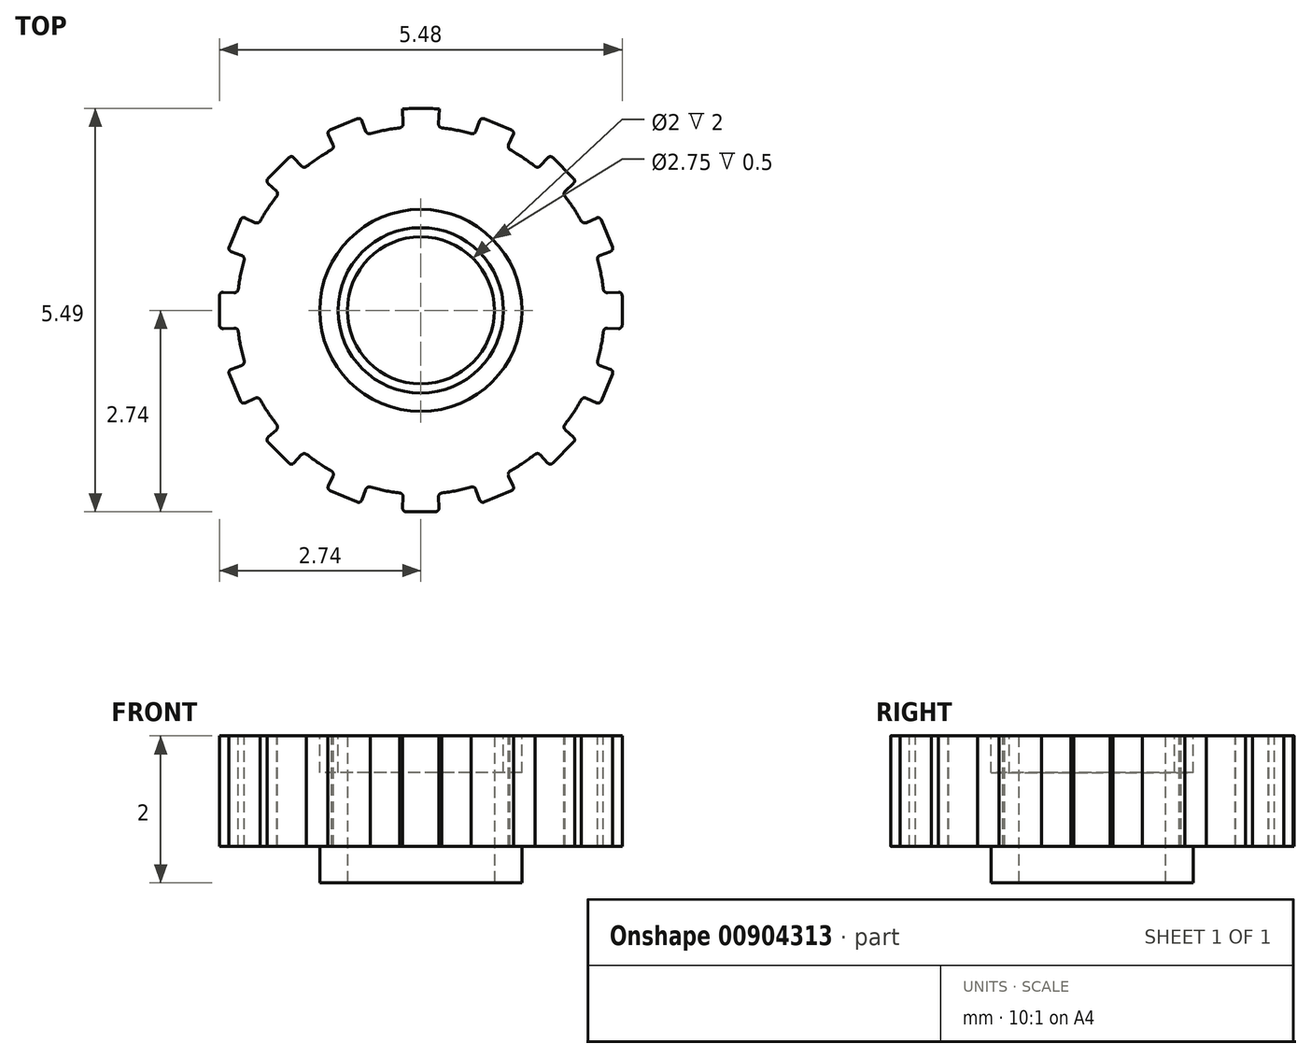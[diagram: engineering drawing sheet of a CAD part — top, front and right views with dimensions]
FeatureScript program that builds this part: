
annotation { "Feature Type Name" : "Feature", "Feature Type Description" : "" }
export const myFeature = defineFeature(function(context is Context, id is Id, definition is map)
    precondition{}
    {
        {
            var Q0;
            Q0=qCreatedBy(makeId("Front.planeOp"),FACE);
            var sketch = newSketch(context, id + "F0", { "sketchPlane" : qUnion([Q0])});
            skLineSegment(sketch, "E0.bottom", {"start": v(0, 0) * mm, "end": v(-2.75, 0) * mm});
            skLineSegment(sketch, "E0.top", {"start": v(0, 2) * mm, "end": v(-2.75, 2) * mm});
            skLineSegment(sketch, "E0.left", {"start": v(0, 0) * mm, "end": v(0, 2) * mm});
            skLineSegment(sketch, "E0.right", {"start": v(-2.75, 0) * mm, "end": v(-2.75, 2) * mm});
            skLineSegment(sketch, "E1", {"start": v(-1, 2) * mm, "end": v(-1, 0) * mm});
            skSolve(sketch);
        }
        {
            var Q0;
            {var subQ0=sQuery(id+"F0.wireOp",EDGE,"E0.right");Q0=makeQuery(id+"F0.imprint","IMPRINT",FACE,{"disambiguationData":[TD([[makeQuery(id+"F0.imprint","IMPRINT",EDGE,{"derivedFrom":subQ0}),-1.0]])]});}
            var Q1;
            Q1=sQuery(id+"F0.wireOp",EDGE,"E0.left");
            revolve(context, id + "F1", {"surfaceOperationType" : NewSurfaceOperationType.NEW, "entities" : qUnion([Q0]), "axis" : qUnion([Q1]), "revolveType" : RevolveType.FULL});
        }
        {
            var Q0;
            Q0=makeQuery(id+"F1.opRevolve","SWEPT_FACE",FACE,{"disambiguationData":[OSD([sQuery(id+"F0.wireOp",EDGE,"E0.top")])]});
            var sketch = newSketch(context, id + "F2", { "sketchPlane" : qUnion([Q0])});
            skLineSegment(sketch, "E2", {"start": v(0, 0) * mm, "end": v(0, 2.75) * mm});
            skLineSegment(sketch, "E3", {"start": v(0, 2.74) * mm, "end": v(-0.25, 2.74) * mm});
            skLineSegment(sketch, "E4", {"start": v(-0.25, 2.74) * mm, "end": v(0.25, 2.74) * mm});
            skLineSegment(sketch, "E5.bottom", {"start": v(0.12, 0) * mm, "end": v(-0.12, 0) * mm});
            skLineSegment(sketch, "E5.top", {"start": v(0.12, 0) * mm, "end": v(-0.12, 0) * mm});
            skLineSegment(sketch, "E5.left", {"start": v(0.12, 0) * mm, "end": v(0.12, 0) * mm});
            skLineSegment(sketch, "E5.right", {"start": v(-0.12, 0) * mm, "end": v(-0.12, 0) * mm});
            skPoint(sketch, "E5.middle", {"position": v(0, 0) * mm});
            skLineSegment(sketch, "E6", {"start": v(-0.25, 2.74) * mm, "end": v(-0.12, 0) * mm});
            skLineSegment(sketch, "E7", {"start": v(0.25, 2.74) * mm, "end": v(0.12, 0) * mm});
            skCircle(sketch, "E8", {"center": v(0, 0) * mm, "radius": 2.5 * mm});
            skLineSegment(sketch, "E9", {"start": v(-0.25, 2.74) * mm, "end": v(-0.2, 2.74) * mm});
            skLineSegment(sketch, "E10", {"start": v(-0.2, 2.74) * mm, "end": v(0.2, 2.74) * mm});
            skLineSegment(sketch, "E11", {"start": v(0.2, 2.74) * mm, "end": v(0.25, 2.74) * mm});
            skLineSegment(sketch, "E12", {"start": v(-0.2, 2.74) * mm, "end": v(-0.12, 0) * mm});
            skLineSegment(sketch, "E13", {"start": v(0.2, 2.74) * mm, "end": v(0.12, 0) * mm});
            skLineSegment(sketch, "E14", {"start": v(-0.25, 2.69) * mm, "end": v(0.25, 2.69) * mm});
            skLineSegment(sketch, "E15", {"start": v(-0.25, 2.69) * mm, "end": v(-0.3, 2.69) * mm});
            skLineSegment(sketch, "E16", {"start": v(0.25, 2.69) * mm, "end": v(0.3, 2.69) * mm});
            skLineSegment(sketch, "E17", {"start": v(-0.3, 2.69) * mm, "end": v(-0.12, 0) * mm});
            skLineSegment(sketch, "E18", {"start": v(0.3, 2.69) * mm, "end": v(0.12, 0) * mm});
            skLineSegment(sketch, "E19", {"start": v(-0.24, 2.54) * mm, "end": v(0.2, 2.54) * mm});
            skLineSegment(sketch, "E20", {"start": v(0.2, 2.54) * mm, "end": v(0.24, 2.54) * mm});
            skLineSegment(sketch, "E21", {"start": v(0.24, 2.54) * mm, "end": v(-0.2, 2.54) * mm});
            skArc(sketch, "E22", {"start": v(-0.28, 2.48) * mm, "mid": v(-0.25, 2.5) * mm, "end": v(-0.24, 2.54) * mm});
            skArc(sketch, "E23", {"start": v(-0.2, 2.74) * mm, "mid": v(-0.23, 2.72) * mm, "end": v(-0.25, 2.69) * mm});
            skArc(sketch, "E24", {"start": v(0.25, 2.69) * mm, "mid": v(0.23, 2.72) * mm, "end": v(0.2, 2.74) * mm});
            skArc(sketch, "E25", {"start": v(0.24, 2.54) * mm, "mid": v(0.25, 2.5) * mm, "end": v(0.28, 2.48) * mm});
            skArc(sketch, "E26.1.0", {"start": v(-1.21, 2.19) * mm, "mid": v(-1.2, 2.22) * mm, "end": v(-1.2, 2.25) * mm});
            skLineSegment(sketch, "E26.1.1", {"start": v(-1.28, 2.43) * mm, "end": v(-0.12, -0.05) * mm});
            skArc(sketch, "E26.1.2", {"start": v(-1.23, 2.45) * mm, "mid": v(-1.26, 2.43) * mm, "end": v(-1.26, 2.39) * mm});
            skLineSegment(sketch, "E26.1.3", {"start": v(-1.28, 2.43) * mm, "end": v(-0.82, 2.63) * mm});
            skArc(sketch, "E26.1.4", {"start": v(-0.8, 2.58) * mm, "mid": v(-0.83, 2.6) * mm, "end": v(-0.86, 2.6) * mm});
            skLineSegment(sketch, "E26.1.5", {"start": v(-0.82, 2.63) * mm, "end": v(0.12, 0.05) * mm});
            skArc(sketch, "E26.1.6", {"start": v(-0.75, 2.44) * mm, "mid": v(-0.72, 2.4) * mm, "end": v(-0.69, 2.4) * mm});
            skArc(sketch, "E26.2.0", {"start": v(-1.96, 1.56) * mm, "mid": v(-1.95, 1.6) * mm, "end": v(-1.97, 1.62) * mm});
            skLineSegment(sketch, "E26.2.1", {"start": v(-2.11, 1.76) * mm, "end": v(-0.09, -0.09) * mm});
            skArc(sketch, "E26.2.2", {"start": v(-2.08, 1.8) * mm, "mid": v(-2.1, 1.76) * mm, "end": v(-2.08, 1.73) * mm});
            skLineSegment(sketch, "E26.2.3", {"start": v(-2.11, 1.76) * mm, "end": v(-1.76, 2.11) * mm});
            skArc(sketch, "E26.2.4", {"start": v(-1.73, 2.08) * mm, "mid": v(-1.76, 2.1) * mm, "end": v(-1.8, 2.08) * mm});
            skLineSegment(sketch, "E26.2.5", {"start": v(-1.76, 2.11) * mm, "end": v(0.09, 0.09) * mm});
            skArc(sketch, "E26.2.6", {"start": v(-1.62, 1.97) * mm, "mid": v(-1.6, 1.95) * mm, "end": v(-1.56, 1.96) * mm});
            skArc(sketch, "E27.2.3.0", {"start": v(-2.4, 0.69) * mm, "mid": v(-2.4, 0.72) * mm, "end": v(-2.44, 0.75) * mm});
            skLineSegment(sketch, "E27.4.3.0", {"start": v(-2.63, 0.82) * mm, "end": v(-0.05, -0.12) * mm});
            skArc(sketch, "E27.7.3.0", {"start": v(-2.6, 0.86) * mm, "mid": v(-2.6, 0.83) * mm, "end": v(-2.58, 0.8) * mm});
            skLineSegment(sketch, "E27.11.3.0", {"start": v(-2.63, 0.82) * mm, "end": v(-2.43, 1.28) * mm});
            skArc(sketch, "E27.14.3.0", {"start": v(-2.39, 1.26) * mm, "mid": v(-2.43, 1.26) * mm, "end": v(-2.45, 1.23) * mm});
            skLineSegment(sketch, "E27.18.3.0", {"start": v(-2.43, 1.28) * mm, "end": v(0.05, 0.12) * mm});
            skArc(sketch, "E27.21.3.0", {"start": v(-2.25, 1.2) * mm, "mid": v(-2.22, 1.2) * mm, "end": v(-2.19, 1.21) * mm});
            skArc(sketch, "E27.2.4.0", {"start": v(-2.48, -0.28) * mm, "mid": v(-2.5, -0.25) * mm, "end": v(-2.54, -0.24) * mm});
            skLineSegment(sketch, "E27.4.4.0", {"start": v(-2.74, -0.25) * mm, "end": v(0, -0.12) * mm});
            skArc(sketch, "E27.7.4.0", {"start": v(-2.74, -0.2) * mm, "mid": v(-2.72, -0.23) * mm, "end": v(-2.69, -0.25) * mm});
            skLineSegment(sketch, "E27.11.4.0", {"start": v(-2.74, -0.25) * mm, "end": v(-2.74, 0.25) * mm});
            skArc(sketch, "E27.14.4.0", {"start": v(-2.69, 0.25) * mm, "mid": v(-2.72, 0.23) * mm, "end": v(-2.74, 0.2) * mm});
            skLineSegment(sketch, "E27.18.4.0", {"start": v(-2.74, 0.25) * mm, "end": v(0, 0.12) * mm});
            skArc(sketch, "E27.21.4.0", {"start": v(-2.54, 0.24) * mm, "mid": v(-2.5, 0.25) * mm, "end": v(-2.48, 0.28) * mm});
            skArc(sketch, "E27.2.5.0", {"start": v(-2.19, -1.21) * mm, "mid": v(-2.22, -1.2) * mm, "end": v(-2.25, -1.2) * mm});
            skLineSegment(sketch, "E27.4.5.0", {"start": v(-2.43, -1.28) * mm, "end": v(0.05, -0.12) * mm});
            skArc(sketch, "E27.7.5.0", {"start": v(-2.45, -1.23) * mm, "mid": v(-2.43, -1.26) * mm, "end": v(-2.39, -1.26) * mm});
            skLineSegment(sketch, "E27.11.5.0", {"start": v(-2.43, -1.28) * mm, "end": v(-2.63, -0.82) * mm});
            skArc(sketch, "E27.14.5.0", {"start": v(-2.58, -0.8) * mm, "mid": v(-2.6, -0.83) * mm, "end": v(-2.6, -0.86) * mm});
            skLineSegment(sketch, "E27.18.5.0", {"start": v(-2.63, -0.82) * mm, "end": v(-0.05, 0.12) * mm});
            skArc(sketch, "E27.21.5.0", {"start": v(-2.44, -0.75) * mm, "mid": v(-2.4, -0.72) * mm, "end": v(-2.4, -0.69) * mm});
            skArc(sketch, "E27.2.6.0", {"start": v(-1.56, -1.96) * mm, "mid": v(-1.6, -1.95) * mm, "end": v(-1.62, -1.97) * mm});
            skLineSegment(sketch, "E27.4.6.0", {"start": v(-1.76, -2.11) * mm, "end": v(0.09, -0.09) * mm});
            skArc(sketch, "E27.7.6.0", {"start": v(-1.8, -2.08) * mm, "mid": v(-1.76, -2.1) * mm, "end": v(-1.73, -2.08) * mm});
            skLineSegment(sketch, "E27.11.6.0", {"start": v(-1.76, -2.11) * mm, "end": v(-2.11, -1.76) * mm});
            skArc(sketch, "E27.14.6.0", {"start": v(-2.08, -1.73) * mm, "mid": v(-2.1, -1.76) * mm, "end": v(-2.08, -1.8) * mm});
            skLineSegment(sketch, "E27.18.6.0", {"start": v(-2.11, -1.76) * mm, "end": v(-0.09, 0.09) * mm});
            skArc(sketch, "E27.21.6.0", {"start": v(-1.97, -1.62) * mm, "mid": v(-1.95, -1.6) * mm, "end": v(-1.96, -1.56) * mm});
            skArc(sketch, "E27.2.7.0", {"start": v(-0.69, -2.4) * mm, "mid": v(-0.72, -2.4) * mm, "end": v(-0.75, -2.44) * mm});
            skLineSegment(sketch, "E27.4.7.0", {"start": v(-0.82, -2.63) * mm, "end": v(0.12, -0.05) * mm});
            skArc(sketch, "E27.7.7.0", {"start": v(-0.86, -2.6) * mm, "mid": v(-0.83, -2.6) * mm, "end": v(-0.8, -2.58) * mm});
            skLineSegment(sketch, "E27.11.7.0", {"start": v(-0.82, -2.63) * mm, "end": v(-1.28, -2.43) * mm});
            skArc(sketch, "E27.14.7.0", {"start": v(-1.26, -2.39) * mm, "mid": v(-1.26, -2.43) * mm, "end": v(-1.23, -2.45) * mm});
            skLineSegment(sketch, "E27.18.7.0", {"start": v(-1.28, -2.43) * mm, "end": v(-0.12, 0.05) * mm});
            skArc(sketch, "E27.21.7.0", {"start": v(-1.2, -2.25) * mm, "mid": v(-1.2, -2.22) * mm, "end": v(-1.21, -2.19) * mm});
            skArc(sketch, "E28.2.8.0", {"start": v(0.28, -2.48) * mm, "mid": v(0.25, -2.5) * mm, "end": v(0.24, -2.54) * mm});
            skLineSegment(sketch, "E28.4.8.0", {"start": v(0.25, -2.74) * mm, "end": v(0.12, 0) * mm});
            skArc(sketch, "E28.7.8.0", {"start": v(0.2, -2.74) * mm, "mid": v(0.23, -2.72) * mm, "end": v(0.25, -2.69) * mm});
            skLineSegment(sketch, "E28.11.8.0", {"start": v(0.25, -2.74) * mm, "end": v(-0.25, -2.74) * mm});
            skArc(sketch, "E28.14.8.0", {"start": v(-0.25, -2.69) * mm, "mid": v(-0.23, -2.72) * mm, "end": v(-0.2, -2.74) * mm});
            skLineSegment(sketch, "E28.18.8.0", {"start": v(-0.25, -2.74) * mm, "end": v(-0.12, 0) * mm});
            skArc(sketch, "E28.21.8.0", {"start": v(-0.24, -2.54) * mm, "mid": v(-0.25, -2.5) * mm, "end": v(-0.28, -2.48) * mm});
            skArc(sketch, "E28.2.9.0", {"start": v(1.21, -2.19) * mm, "mid": v(1.2, -2.22) * mm, "end": v(1.2, -2.25) * mm});
            skLineSegment(sketch, "E28.4.9.0", {"start": v(1.28, -2.43) * mm, "end": v(0.12, 0.05) * mm});
            skArc(sketch, "E28.7.9.0", {"start": v(1.23, -2.45) * mm, "mid": v(1.26, -2.43) * mm, "end": v(1.26, -2.39) * mm});
            skLineSegment(sketch, "E28.11.9.0", {"start": v(1.28, -2.43) * mm, "end": v(0.82, -2.63) * mm});
            skArc(sketch, "E28.14.9.0", {"start": v(0.8, -2.58) * mm, "mid": v(0.83, -2.6) * mm, "end": v(0.86, -2.6) * mm});
            skLineSegment(sketch, "E28.18.9.0", {"start": v(0.82, -2.63) * mm, "end": v(-0.12, -0.05) * mm});
            skArc(sketch, "E28.21.9.0", {"start": v(0.75, -2.44) * mm, "mid": v(0.72, -2.4) * mm, "end": v(0.69, -2.4) * mm});
            skArc(sketch, "E28.2.10.0", {"start": v(1.96, -1.56) * mm, "mid": v(1.95, -1.6) * mm, "end": v(1.97, -1.62) * mm});
            skLineSegment(sketch, "E28.4.10.0", {"start": v(2.11, -1.76) * mm, "end": v(0.09, 0.09) * mm});
            skArc(sketch, "E28.7.10.0", {"start": v(2.08, -1.8) * mm, "mid": v(2.1, -1.76) * mm, "end": v(2.08, -1.73) * mm});
            skLineSegment(sketch, "E28.11.10.0", {"start": v(2.11, -1.76) * mm, "end": v(1.76, -2.11) * mm});
            skArc(sketch, "E28.14.10.0", {"start": v(1.73, -2.08) * mm, "mid": v(1.76, -2.1) * mm, "end": v(1.8, -2.08) * mm});
            skLineSegment(sketch, "E28.18.10.0", {"start": v(1.76, -2.11) * mm, "end": v(-0.09, -0.09) * mm});
            skArc(sketch, "E28.21.10.0", {"start": v(1.62, -1.97) * mm, "mid": v(1.6, -1.95) * mm, "end": v(1.56, -1.96) * mm});
            skArc(sketch, "E28.2.11.0", {"start": v(2.4, -0.69) * mm, "mid": v(2.4, -0.72) * mm, "end": v(2.44, -0.75) * mm});
            skLineSegment(sketch, "E28.4.11.0", {"start": v(2.63, -0.82) * mm, "end": v(0.05, 0.12) * mm});
            skArc(sketch, "E28.7.11.0", {"start": v(2.6, -0.86) * mm, "mid": v(2.6, -0.83) * mm, "end": v(2.58, -0.8) * mm});
            skLineSegment(sketch, "E28.11.11.0", {"start": v(2.63, -0.82) * mm, "end": v(2.43, -1.28) * mm});
            skArc(sketch, "E28.14.11.0", {"start": v(2.39, -1.26) * mm, "mid": v(2.43, -1.26) * mm, "end": v(2.45, -1.23) * mm});
            skLineSegment(sketch, "E28.18.11.0", {"start": v(2.43, -1.28) * mm, "end": v(-0.05, -0.12) * mm});
            skArc(sketch, "E28.21.11.0", {"start": v(2.25, -1.2) * mm, "mid": v(2.22, -1.2) * mm, "end": v(2.19, -1.21) * mm});
            skArc(sketch, "E28.2.12.0", {"start": v(2.48, 0.28) * mm, "mid": v(2.5, 0.25) * mm, "end": v(2.54, 0.24) * mm});
            skLineSegment(sketch, "E28.4.12.0", {"start": v(2.74, 0.25) * mm, "end": v(0, 0.13) * mm});
            skArc(sketch, "E28.7.12.0", {"start": v(2.74, 0.2) * mm, "mid": v(2.72, 0.23) * mm, "end": v(2.69, 0.25) * mm});
            skLineSegment(sketch, "E28.11.12.0", {"start": v(2.74, 0.25) * mm, "end": v(2.74, -0.25) * mm});
            skArc(sketch, "E28.14.12.0", {"start": v(2.69, -0.25) * mm, "mid": v(2.72, -0.23) * mm, "end": v(2.74, -0.2) * mm});
            skLineSegment(sketch, "E28.18.12.0", {"start": v(2.74, -0.25) * mm, "end": v(0, -0.12) * mm});
            skArc(sketch, "E28.21.12.0", {"start": v(2.54, -0.24) * mm, "mid": v(2.5, -0.25) * mm, "end": v(2.48, -0.28) * mm});
            skArc(sketch, "E28.2.13.0", {"start": v(2.19, 1.21) * mm, "mid": v(2.22, 1.2) * mm, "end": v(2.25, 1.2) * mm});
            skLineSegment(sketch, "E28.4.13.0", {"start": v(2.43, 1.28) * mm, "end": v(-0.05, 0.12) * mm});
            skArc(sketch, "E28.7.13.0", {"start": v(2.45, 1.23) * mm, "mid": v(2.43, 1.26) * mm, "end": v(2.39, 1.26) * mm});
            skLineSegment(sketch, "E28.11.13.0", {"start": v(2.43, 1.28) * mm, "end": v(2.63, 0.82) * mm});
            skArc(sketch, "E28.14.13.0", {"start": v(2.58, 0.8) * mm, "mid": v(2.6, 0.83) * mm, "end": v(2.6, 0.86) * mm});
            skLineSegment(sketch, "E28.18.13.0", {"start": v(2.63, 0.82) * mm, "end": v(0.05, -0.12) * mm});
            skArc(sketch, "E28.21.13.0", {"start": v(2.44, 0.75) * mm, "mid": v(2.4, 0.72) * mm, "end": v(2.4, 0.69) * mm});
            skArc(sketch, "E29.2.14.0", {"start": v(1.56, 1.96) * mm, "mid": v(1.6, 1.95) * mm, "end": v(1.62, 1.97) * mm});
            skLineSegment(sketch, "E29.4.14.0", {"start": v(1.76, 2.11) * mm, "end": v(-0.09, 0.09) * mm});
            skArc(sketch, "E29.7.14.0", {"start": v(1.8, 2.08) * mm, "mid": v(1.76, 2.1) * mm, "end": v(1.73, 2.08) * mm});
            skLineSegment(sketch, "E29.11.14.0", {"start": v(1.76, 2.11) * mm, "end": v(2.11, 1.76) * mm});
            skArc(sketch, "E29.14.14.0", {"start": v(2.08, 1.73) * mm, "mid": v(2.1, 1.76) * mm, "end": v(2.08, 1.8) * mm});
            skLineSegment(sketch, "E29.18.14.0", {"start": v(2.11, 1.76) * mm, "end": v(0.09, -0.09) * mm});
            skArc(sketch, "E29.21.14.0", {"start": v(1.97, 1.62) * mm, "mid": v(1.95, 1.6) * mm, "end": v(1.96, 1.56) * mm});
            skArc(sketch, "E29.2.15.0", {"start": v(0.69, 2.4) * mm, "mid": v(0.72, 2.4) * mm, "end": v(0.75, 2.44) * mm});
            skLineSegment(sketch, "E29.4.15.0", {"start": v(0.82, 2.63) * mm, "end": v(-0.12, 0.05) * mm});
            skArc(sketch, "E29.7.15.0", {"start": v(0.86, 2.6) * mm, "mid": v(0.83, 2.6) * mm, "end": v(0.8, 2.58) * mm});
            skLineSegment(sketch, "E29.11.15.0", {"start": v(0.82, 2.63) * mm, "end": v(1.28, 2.43) * mm});
            skArc(sketch, "E29.14.15.0", {"start": v(1.26, 2.39) * mm, "mid": v(1.26, 2.43) * mm, "end": v(1.23, 2.45) * mm});
            skLineSegment(sketch, "E29.18.15.0", {"start": v(1.28, 2.43) * mm, "end": v(0.12, -0.05) * mm});
            skArc(sketch, "E29.21.15.0", {"start": v(1.2, 2.25) * mm, "mid": v(1.2, 2.22) * mm, "end": v(1.21, 2.19) * mm});
            skSolve(sketch);
        }
        {
            var Q0;
            {var subQ1=sQuery(id+"F2.wireOp",EDGE,"E15");Q0=makeQuery(id+"F2.imprint","IMPRINT",FACE,{"disambiguationData":[TD([[makeQuery(id+"F2.imprint","IMPRINT",EDGE,{"derivedFrom":subQ1}),-1.0]])]});}
            var Q1;
            {var subQ0=sQuery(id+"F2.wireOp",EDGE,"E15");Q1=makeQuery(id+"F2.imprint","IMPRINT",FACE,{"disambiguationData":[TD([[makeQuery(id+"F2.imprint","IMPRINT",EDGE,{"derivedFrom":subQ0}),1.0]])]});}
            var Q2;
            {var subQ0=sQuery(id+"F2.wireOp",EDGE,"E9");Q2=makeQuery(id+"F2.imprint","IMPRINT",FACE,{"disambiguationData":[TD([[makeQuery(id+"F2.imprint","IMPRINT",EDGE,{"derivedFrom":subQ0}),-1.0]])]});}
            var Q3;
            {var subQ5=sQuery(id+"F2.wireOp",EDGE,"E9");Q3=makeQuery(id+"F2.imprint","IMPRINT",FACE,{"disambiguationData":[TD([[makeQuery(id+"F2.imprint","IMPRINT",EDGE,{"derivedFrom":subQ5}),1.0]])]});}
            var Q4;
            {var subQ5=sQuery(id+"F2.wireOp",EDGE,"E11");Q4=makeQuery(id+"F2.imprint","IMPRINT",FACE,{"disambiguationData":[TD([[makeQuery(id+"F2.imprint","IMPRINT",EDGE,{"derivedFrom":subQ5}),1.0]])]});}
            var Q5;
            {var subQ0=sQuery(id+"F2.wireOp",EDGE,"E11");Q5=makeQuery(id+"F2.imprint","IMPRINT",FACE,{"disambiguationData":[TD([[makeQuery(id+"F2.imprint","IMPRINT",EDGE,{"derivedFrom":subQ0}),-1.0]])]});}
            var Q6;
            {var subQ0=sQuery(id+"F2.wireOp",EDGE,"E16");Q6=makeQuery(id+"F2.imprint","IMPRINT",FACE,{"disambiguationData":[TD([[makeQuery(id+"F2.imprint","IMPRINT",EDGE,{"derivedFrom":subQ0}),1.0]])]});}
            var Q7;
            {var subQ0=sQuery(id+"F2.wireOp",EDGE,"E16");Q7=makeQuery(id+"F2.imprint","IMPRINT",FACE,{"disambiguationData":[TD([[makeQuery(id+"F2.imprint","IMPRINT",EDGE,{"derivedFrom":subQ0}),-1.0]])]});}
            var Q8;
            {var subQ3=sQuery(id+"F2.wireOp",EDGE,"E27.7.7.0");Q8=makeQuery(id+"F2.imprint","IMPRINT",FACE,{"disambiguationData":[TD([[makeQuery(id+"F2.imprint","IMPRINT",EDGE,{"derivedFrom":subQ3}),-1.0]])]});}
            var Q9;
            {var subQ0=sQuery(id+"F2.wireOp",EDGE,"E27.11.7.0");var subQ3=makeQuery(id+"F2.imprint","INTERSECT",VERTEX,{"derivedFrom":[sQuery(id+"F2.wireOp",EDGE,"E27.7.7.0"),subQ0]});Q9=makeQuery(id+"F2.imprint","IMPRINT",FACE,{"disambiguationData":[TD([[makeQuery(id+"F2.imprint","IMPRINT",EDGE,{"disambiguationData":[TD([[subQ3,-1.0]])],"derivedFrom":subQ0}),1.0]])]});}
            var Q10;
            {var subQ3=sQuery(id+"F2.wireOp",EDGE,"E27.14.7.0");Q10=makeQuery(id+"F2.imprint","IMPRINT",FACE,{"disambiguationData":[TD([[makeQuery(id+"F2.imprint","IMPRINT",EDGE,{"derivedFrom":subQ3}),-1.0]])]});}
            var Q11;
            {var subQ4=sQuery(id+"F2.wireOp",EDGE,"E27.2.6.0");Q11=makeQuery(id+"F2.imprint","IMPRINT",FACE,{"disambiguationData":[TD([[makeQuery(id+"F2.imprint","IMPRINT",EDGE,{"derivedFrom":subQ4}),1.0]])]});}
            var Q12;
            {var subQ3=sQuery(id+"F2.wireOp",EDGE,"E27.7.6.0");Q12=makeQuery(id+"F2.imprint","IMPRINT",FACE,{"disambiguationData":[TD([[makeQuery(id+"F2.imprint","IMPRINT",EDGE,{"derivedFrom":subQ3}),-1.0]])]});}
            var Q13;
            {var subQ0=sQuery(id+"F2.wireOp",EDGE,"E27.11.6.0");var subQ3=makeQuery(id+"F2.imprint","INTERSECT",VERTEX,{"derivedFrom":[sQuery(id+"F2.wireOp",EDGE,"E27.7.6.0"),subQ0]});Q13=makeQuery(id+"F2.imprint","IMPRINT",FACE,{"disambiguationData":[TD([[makeQuery(id+"F2.imprint","IMPRINT",EDGE,{"disambiguationData":[TD([[subQ3,-1.0]])],"derivedFrom":subQ0}),1.0]])]});}
            var Q14;
            {var subQ1=sQuery(id+"F2.wireOp",EDGE,"E27.2.5.0");Q14=makeQuery(id+"F2.imprint","IMPRINT",FACE,{"disambiguationData":[TD([[makeQuery(id+"F2.imprint","IMPRINT",EDGE,{"derivedFrom":subQ1}),1.0]])]});}
            var Q15;
            {var subQ3=sQuery(id+"F2.wireOp",EDGE,"E27.14.6.0");Q15=makeQuery(id+"F2.imprint","IMPRINT",FACE,{"disambiguationData":[TD([[makeQuery(id+"F2.imprint","IMPRINT",EDGE,{"derivedFrom":subQ3}),-1.0]])]});}
            var Q16;
            {var subQ0=sQuery(id+"F2.wireOp",EDGE,"E27.11.5.0");var subQ3=makeQuery(id+"F2.imprint","INTERSECT",VERTEX,{"derivedFrom":[sQuery(id+"F2.wireOp",EDGE,"E27.7.5.0"),subQ0]});Q16=makeQuery(id+"F2.imprint","IMPRINT",FACE,{"disambiguationData":[TD([[makeQuery(id+"F2.imprint","IMPRINT",EDGE,{"disambiguationData":[TD([[subQ3,-1.0]])],"derivedFrom":subQ0}),1.0]])]});}
            var Q17;
            {var subQ3=sQuery(id+"F2.wireOp",EDGE,"E27.7.5.0");Q17=makeQuery(id+"F2.imprint","IMPRINT",FACE,{"disambiguationData":[TD([[makeQuery(id+"F2.imprint","IMPRINT",EDGE,{"derivedFrom":subQ3}),-1.0]])]});}
            var Q18;
            {var subQ3=sQuery(id+"F2.wireOp",EDGE,"E27.14.5.0");Q18=makeQuery(id+"F2.imprint","IMPRINT",FACE,{"disambiguationData":[TD([[makeQuery(id+"F2.imprint","IMPRINT",EDGE,{"derivedFrom":subQ3}),-1.0]])]});}
            var Q19;
            {var subQ4=sQuery(id+"F2.wireOp",EDGE,"E27.2.4.0");Q19=makeQuery(id+"F2.imprint","IMPRINT",FACE,{"disambiguationData":[TD([[makeQuery(id+"F2.imprint","IMPRINT",EDGE,{"derivedFrom":subQ4}),1.0]])]});}
            var Q20;
            {var subQ3=sQuery(id+"F2.wireOp",EDGE,"E27.7.4.0");Q20=makeQuery(id+"F2.imprint","IMPRINT",FACE,{"disambiguationData":[TD([[makeQuery(id+"F2.imprint","IMPRINT",EDGE,{"derivedFrom":subQ3}),-1.0]])]});}
            var Q21;
            {var subQ0=sQuery(id+"F2.wireOp",EDGE,"E27.11.4.0");var subQ3=makeQuery(id+"F2.imprint","INTERSECT",VERTEX,{"derivedFrom":[sQuery(id+"F2.wireOp",EDGE,"E27.7.4.0"),subQ0]});Q21=makeQuery(id+"F2.imprint","IMPRINT",FACE,{"disambiguationData":[TD([[makeQuery(id+"F2.imprint","IMPRINT",EDGE,{"disambiguationData":[TD([[subQ3,-1.0]])],"derivedFrom":subQ0}),1.0]])]});}
            var Q22;
            {var subQ3=sQuery(id+"F2.wireOp",EDGE,"E27.14.4.0");Q22=makeQuery(id+"F2.imprint","IMPRINT",FACE,{"disambiguationData":[TD([[makeQuery(id+"F2.imprint","IMPRINT",EDGE,{"derivedFrom":subQ3}),-1.0]])]});}
            var Q23;
            {var subQ1=sQuery(id+"F2.wireOp",EDGE,"E27.2.3.0");Q23=makeQuery(id+"F2.imprint","IMPRINT",FACE,{"disambiguationData":[TD([[makeQuery(id+"F2.imprint","IMPRINT",EDGE,{"derivedFrom":subQ1}),1.0]])]});}
            var Q24;
            {var subQ3=sQuery(id+"F2.wireOp",EDGE,"E27.7.3.0");Q24=makeQuery(id+"F2.imprint","IMPRINT",FACE,{"disambiguationData":[TD([[makeQuery(id+"F2.imprint","IMPRINT",EDGE,{"derivedFrom":subQ3}),-1.0]])]});}
            var Q25;
            {var subQ0=sQuery(id+"F2.wireOp",EDGE,"E27.11.3.0");var subQ3=makeQuery(id+"F2.imprint","INTERSECT",VERTEX,{"derivedFrom":[sQuery(id+"F2.wireOp",EDGE,"E27.7.3.0"),subQ0]});Q25=makeQuery(id+"F2.imprint","IMPRINT",FACE,{"disambiguationData":[TD([[makeQuery(id+"F2.imprint","IMPRINT",EDGE,{"disambiguationData":[TD([[subQ3,-1.0]])],"derivedFrom":subQ0}),1.0]])]});}
            var Q26;
            {var subQ3=sQuery(id+"F2.wireOp",EDGE,"E27.14.3.0");Q26=makeQuery(id+"F2.imprint","IMPRINT",FACE,{"disambiguationData":[TD([[makeQuery(id+"F2.imprint","IMPRINT",EDGE,{"derivedFrom":subQ3}),-1.0]])]});}
            var Q27;
            {var subQ0=sQuery(id+"F2.wireOp",EDGE,"E26.2.3");var subQ3=makeQuery(id+"F2.imprint","INTERSECT",VERTEX,{"derivedFrom":[sQuery(id+"F2.wireOp",EDGE,"E26.2.2"),subQ0]});Q27=makeQuery(id+"F2.imprint","IMPRINT",FACE,{"disambiguationData":[TD([[makeQuery(id+"F2.imprint","IMPRINT",EDGE,{"disambiguationData":[TD([[subQ3,-1.0]])],"derivedFrom":subQ0}),1.0]])]});}
            var Q28;
            {var subQ3=sQuery(id+"F2.wireOp",EDGE,"E26.2.2");Q28=makeQuery(id+"F2.imprint","IMPRINT",FACE,{"disambiguationData":[TD([[makeQuery(id+"F2.imprint","IMPRINT",EDGE,{"derivedFrom":subQ3}),-1.0]])]});}
            var Q29;
            {var subQ1=sQuery(id+"F2.wireOp",EDGE,"E26.2.0");Q29=makeQuery(id+"F2.imprint","IMPRINT",FACE,{"disambiguationData":[TD([[makeQuery(id+"F2.imprint","IMPRINT",EDGE,{"derivedFrom":subQ1}),1.0]])]});}
            var Q30;
            {var subQ3=sQuery(id+"F2.wireOp",EDGE,"E26.2.4");Q30=makeQuery(id+"F2.imprint","IMPRINT",FACE,{"disambiguationData":[TD([[makeQuery(id+"F2.imprint","IMPRINT",EDGE,{"derivedFrom":subQ3}),-1.0]])]});}
            var Q31;
            {var subQ1=sQuery(id+"F2.wireOp",EDGE,"E26.1.0");Q31=makeQuery(id+"F2.imprint","IMPRINT",FACE,{"disambiguationData":[TD([[makeQuery(id+"F2.imprint","IMPRINT",EDGE,{"derivedFrom":subQ1}),1.0]])]});}
            var Q32;
            {var subQ3=sQuery(id+"F2.wireOp",EDGE,"E26.1.2");Q32=makeQuery(id+"F2.imprint","IMPRINT",FACE,{"disambiguationData":[TD([[makeQuery(id+"F2.imprint","IMPRINT",EDGE,{"derivedFrom":subQ3}),-1.0]])]});}
            var Q33;
            {var subQ3=sQuery(id+"F2.wireOp",EDGE,"E26.1.4");Q33=makeQuery(id+"F2.imprint","IMPRINT",FACE,{"disambiguationData":[TD([[makeQuery(id+"F2.imprint","IMPRINT",EDGE,{"derivedFrom":subQ3}),-1.0]])]});}
            var Q34;
            {var subQ0=sQuery(id+"F2.wireOp",EDGE,"E26.1.3");var subQ3=makeQuery(id+"F2.imprint","INTERSECT",VERTEX,{"derivedFrom":[sQuery(id+"F2.wireOp",EDGE,"E26.1.2"),subQ0]});Q34=makeQuery(id+"F2.imprint","IMPRINT",FACE,{"disambiguationData":[TD([[makeQuery(id+"F2.imprint","IMPRINT",EDGE,{"disambiguationData":[TD([[subQ3,-1.0]])],"derivedFrom":subQ0}),1.0]])]});}
            var Q35;
            {var subQ3=sQuery(id+"F2.wireOp",EDGE,"E28.7.13.0");Q35=makeQuery(id+"F2.imprint","IMPRINT",FACE,{"disambiguationData":[TD([[makeQuery(id+"F2.imprint","IMPRINT",EDGE,{"derivedFrom":subQ3}),-1.0]])]});}
            var Q36;
            {var subQ0=sQuery(id+"F2.wireOp",EDGE,"E28.11.13.0");var subQ3=makeQuery(id+"F2.imprint","INTERSECT",VERTEX,{"derivedFrom":[sQuery(id+"F2.wireOp",EDGE,"E28.7.13.0"),subQ0]});Q36=makeQuery(id+"F2.imprint","IMPRINT",FACE,{"disambiguationData":[TD([[makeQuery(id+"F2.imprint","IMPRINT",EDGE,{"disambiguationData":[TD([[subQ3,-1.0]])],"derivedFrom":subQ0}),1.0]])]});}
            var Q37;
            {var subQ3=sQuery(id+"F2.wireOp",EDGE,"E28.14.13.0");Q37=makeQuery(id+"F2.imprint","IMPRINT",FACE,{"disambiguationData":[TD([[makeQuery(id+"F2.imprint","IMPRINT",EDGE,{"derivedFrom":subQ3}),-1.0]])]});}
            var Q38;
            {var subQ1=sQuery(id+"F2.wireOp",EDGE,"E28.2.12.0");Q38=makeQuery(id+"F2.imprint","IMPRINT",FACE,{"disambiguationData":[TD([[makeQuery(id+"F2.imprint","IMPRINT",EDGE,{"derivedFrom":subQ1}),1.0]])]});}
            var Q39;
            {var subQ3=sQuery(id+"F2.wireOp",EDGE,"E28.7.12.0");Q39=makeQuery(id+"F2.imprint","IMPRINT",FACE,{"disambiguationData":[TD([[makeQuery(id+"F2.imprint","IMPRINT",EDGE,{"derivedFrom":subQ3}),-1.0]])]});}
            var Q40;
            {var subQ0=sQuery(id+"F2.wireOp",EDGE,"E28.11.12.0");var subQ3=makeQuery(id+"F2.imprint","INTERSECT",VERTEX,{"derivedFrom":[sQuery(id+"F2.wireOp",EDGE,"E28.7.12.0"),subQ0]});Q40=makeQuery(id+"F2.imprint","IMPRINT",FACE,{"disambiguationData":[TD([[makeQuery(id+"F2.imprint","IMPRINT",EDGE,{"disambiguationData":[TD([[subQ3,-1.0]])],"derivedFrom":subQ0}),1.0]])]});}
            var Q41;
            {var subQ3=sQuery(id+"F2.wireOp",EDGE,"E28.14.12.0");Q41=makeQuery(id+"F2.imprint","IMPRINT",FACE,{"disambiguationData":[TD([[makeQuery(id+"F2.imprint","IMPRINT",EDGE,{"derivedFrom":subQ3}),-1.0]])]});}
            var Q42;
            {var subQ1=sQuery(id+"F2.wireOp",EDGE,"E28.2.11.0");Q42=makeQuery(id+"F2.imprint","IMPRINT",FACE,{"disambiguationData":[TD([[makeQuery(id+"F2.imprint","IMPRINT",EDGE,{"derivedFrom":subQ1}),1.0]])]});}
            var Q43;
            {var subQ3=sQuery(id+"F2.wireOp",EDGE,"E28.7.11.0");Q43=makeQuery(id+"F2.imprint","IMPRINT",FACE,{"disambiguationData":[TD([[makeQuery(id+"F2.imprint","IMPRINT",EDGE,{"derivedFrom":subQ3}),-1.0]])]});}
            var Q44;
            {var subQ0=sQuery(id+"F2.wireOp",EDGE,"E28.11.11.0");var subQ3=makeQuery(id+"F2.imprint","INTERSECT",VERTEX,{"derivedFrom":[sQuery(id+"F2.wireOp",EDGE,"E28.7.11.0"),subQ0]});Q44=makeQuery(id+"F2.imprint","IMPRINT",FACE,{"disambiguationData":[TD([[makeQuery(id+"F2.imprint","IMPRINT",EDGE,{"disambiguationData":[TD([[subQ3,-1.0]])],"derivedFrom":subQ0}),1.0]])]});}
            var Q45;
            {var subQ3=sQuery(id+"F2.wireOp",EDGE,"E28.7.10.0");Q45=makeQuery(id+"F2.imprint","IMPRINT",FACE,{"disambiguationData":[TD([[makeQuery(id+"F2.imprint","IMPRINT",EDGE,{"derivedFrom":subQ3}),-1.0]])]});}
            var Q46;
            {var subQ0=sQuery(id+"F2.wireOp",EDGE,"E28.11.10.0");var subQ3=makeQuery(id+"F2.imprint","INTERSECT",VERTEX,{"derivedFrom":[sQuery(id+"F2.wireOp",EDGE,"E28.7.10.0"),subQ0]});Q46=makeQuery(id+"F2.imprint","IMPRINT",FACE,{"disambiguationData":[TD([[makeQuery(id+"F2.imprint","IMPRINT",EDGE,{"disambiguationData":[TD([[subQ3,-1.0]])],"derivedFrom":subQ0}),1.0]])]});}
            var Q47;
            {var subQ3=sQuery(id+"F2.wireOp",EDGE,"E28.7.9.0");Q47=makeQuery(id+"F2.imprint","IMPRINT",FACE,{"disambiguationData":[TD([[makeQuery(id+"F2.imprint","IMPRINT",EDGE,{"derivedFrom":subQ3}),-1.0]])]});}
            var Q48;
            {var subQ0=sQuery(id+"F2.wireOp",EDGE,"E28.11.9.0");var subQ3=makeQuery(id+"F2.imprint","INTERSECT",VERTEX,{"derivedFrom":[sQuery(id+"F2.wireOp",EDGE,"E28.7.9.0"),subQ0]});Q48=makeQuery(id+"F2.imprint","IMPRINT",FACE,{"disambiguationData":[TD([[makeQuery(id+"F2.imprint","IMPRINT",EDGE,{"disambiguationData":[TD([[subQ3,-1.0]])],"derivedFrom":subQ0}),1.0]])]});}
            var Q49;
            {var subQ3=sQuery(id+"F2.wireOp",EDGE,"E28.14.9.0");Q49=makeQuery(id+"F2.imprint","IMPRINT",FACE,{"disambiguationData":[TD([[makeQuery(id+"F2.imprint","IMPRINT",EDGE,{"derivedFrom":subQ3}),-1.0]])]});}
            var Q50;
            {var subQ1=sQuery(id+"F2.wireOp",EDGE,"E28.2.8.0");Q50=makeQuery(id+"F2.imprint","IMPRINT",FACE,{"disambiguationData":[TD([[makeQuery(id+"F2.imprint","IMPRINT",EDGE,{"derivedFrom":subQ1}),1.0]])]});}
            var Q51;
            {var subQ1=sQuery(id+"F2.wireOp",EDGE,"E28.2.9.0");Q51=makeQuery(id+"F2.imprint","IMPRINT",FACE,{"disambiguationData":[TD([[makeQuery(id+"F2.imprint","IMPRINT",EDGE,{"derivedFrom":subQ1}),1.0]])]});}
            var Q52;
            {var subQ1=sQuery(id+"F2.wireOp",EDGE,"E28.2.10.0");Q52=makeQuery(id+"F2.imprint","IMPRINT",FACE,{"disambiguationData":[TD([[makeQuery(id+"F2.imprint","IMPRINT",EDGE,{"derivedFrom":subQ1}),1.0]])]});}
            var Q53;
            {var subQ3=sQuery(id+"F2.wireOp",EDGE,"E28.14.10.0");Q53=makeQuery(id+"F2.imprint","IMPRINT",FACE,{"disambiguationData":[TD([[makeQuery(id+"F2.imprint","IMPRINT",EDGE,{"derivedFrom":subQ3}),-1.0]])]});}
            var Q54;
            {var subQ3=sQuery(id+"F2.wireOp",EDGE,"E28.14.11.0");Q54=makeQuery(id+"F2.imprint","IMPRINT",FACE,{"disambiguationData":[TD([[makeQuery(id+"F2.imprint","IMPRINT",EDGE,{"derivedFrom":subQ3}),-1.0]])]});}
            var Q55;
            {var subQ3=sQuery(id+"F2.wireOp",EDGE,"E28.7.8.0");Q55=makeQuery(id+"F2.imprint","IMPRINT",FACE,{"disambiguationData":[TD([[makeQuery(id+"F2.imprint","IMPRINT",EDGE,{"derivedFrom":subQ3}),-1.0]])]});}
            var Q56;
            {var subQ0=sQuery(id+"F2.wireOp",EDGE,"E28.11.8.0");var subQ3=makeQuery(id+"F2.imprint","INTERSECT",VERTEX,{"derivedFrom":[sQuery(id+"F2.wireOp",EDGE,"E28.7.8.0"),subQ0]});Q56=makeQuery(id+"F2.imprint","IMPRINT",FACE,{"disambiguationData":[TD([[makeQuery(id+"F2.imprint","IMPRINT",EDGE,{"disambiguationData":[TD([[subQ3,-1.0]])],"derivedFrom":subQ0}),1.0]])]});}
            var Q57;
            {var subQ3=sQuery(id+"F2.wireOp",EDGE,"E28.14.8.0");Q57=makeQuery(id+"F2.imprint","IMPRINT",FACE,{"disambiguationData":[TD([[makeQuery(id+"F2.imprint","IMPRINT",EDGE,{"derivedFrom":subQ3}),-1.0]])]});}
            var Q58;
            {var subQ1=sQuery(id+"F2.wireOp",EDGE,"E27.2.7.0");Q58=makeQuery(id+"F2.imprint","IMPRINT",FACE,{"disambiguationData":[TD([[makeQuery(id+"F2.imprint","IMPRINT",EDGE,{"derivedFrom":subQ1}),1.0]])]});}
            var Q59;
            {var subQ4=sQuery(id+"F2.wireOp",EDGE,"E28.2.13.0");Q59=makeQuery(id+"F2.imprint","IMPRINT",FACE,{"disambiguationData":[TD([[makeQuery(id+"F2.imprint","IMPRINT",EDGE,{"derivedFrom":subQ4}),1.0]])]});}
            var Q60;
            {var subQ3=sQuery(id+"F2.wireOp",EDGE,"E29.14.14.0");Q60=makeQuery(id+"F2.imprint","IMPRINT",FACE,{"disambiguationData":[TD([[makeQuery(id+"F2.imprint","IMPRINT",EDGE,{"derivedFrom":subQ3}),-1.0]])]});}
            var Q61;
            {var subQ0=sQuery(id+"F2.wireOp",EDGE,"E29.11.14.0");var subQ3=makeQuery(id+"F2.imprint","INTERSECT",VERTEX,{"derivedFrom":[sQuery(id+"F2.wireOp",EDGE,"E29.7.14.0"),subQ0]});Q61=makeQuery(id+"F2.imprint","IMPRINT",FACE,{"disambiguationData":[TD([[makeQuery(id+"F2.imprint","IMPRINT",EDGE,{"disambiguationData":[TD([[subQ3,-1.0]])],"derivedFrom":subQ0}),1.0]])]});}
            var Q62;
            {var subQ3=sQuery(id+"F2.wireOp",EDGE,"E29.7.14.0");Q62=makeQuery(id+"F2.imprint","IMPRINT",FACE,{"disambiguationData":[TD([[makeQuery(id+"F2.imprint","IMPRINT",EDGE,{"derivedFrom":subQ3}),-1.0]])]});}
            var Q63;
            {var subQ1=sQuery(id+"F2.wireOp",EDGE,"E29.2.14.0");Q63=makeQuery(id+"F2.imprint","IMPRINT",FACE,{"disambiguationData":[TD([[makeQuery(id+"F2.imprint","IMPRINT",EDGE,{"derivedFrom":subQ1}),1.0]])]});}
            var Q64;
            {var subQ0=sQuery(id+"F2.wireOp",EDGE,"E29.11.15.0");var subQ3=makeQuery(id+"F2.imprint","INTERSECT",VERTEX,{"derivedFrom":[sQuery(id+"F2.wireOp",EDGE,"E29.7.15.0"),subQ0]});Q64=makeQuery(id+"F2.imprint","IMPRINT",FACE,{"disambiguationData":[TD([[makeQuery(id+"F2.imprint","IMPRINT",EDGE,{"disambiguationData":[TD([[subQ3,-1.0]])],"derivedFrom":subQ0}),1.0]])]});}
            var Q65;
            {var subQ3=sQuery(id+"F2.wireOp",EDGE,"E29.7.15.0");Q65=makeQuery(id+"F2.imprint","IMPRINT",FACE,{"disambiguationData":[TD([[makeQuery(id+"F2.imprint","IMPRINT",EDGE,{"derivedFrom":subQ3}),-1.0]])]});}
            var Q66;
            {var subQ3=sQuery(id+"F2.wireOp",EDGE,"E29.14.15.0");Q66=makeQuery(id+"F2.imprint","IMPRINT",FACE,{"disambiguationData":[TD([[makeQuery(id+"F2.imprint","IMPRINT",EDGE,{"derivedFrom":subQ3}),-1.0]])]});}
            extrude(context, id + "F3", {"entities" : qUnion([Q0, Q1, Q2, Q3, Q4, Q5, Q6, Q7, Q8, Q9, Q10, Q11, Q12, Q13, Q14, Q15, Q16, Q17, Q18, Q19, Q20, Q21, Q22, Q23, Q24, Q25, Q26, Q27, Q28, Q29, Q30, Q31, Q32, Q33, Q34, Q35, Q36, Q37, Q38, Q39, Q40, Q41, Q42, Q43, Q44, Q45, Q46, Q47, Q48, Q49, Q50, Q51, Q52, Q53, Q54, Q55, Q56, Q57, Q58, Q59, Q60, Q61, Q62, Q63, Q64, Q65, Q66]), "operationType" : NewBodyOperationType.REMOVE, "oppositeDirection" : true, "depth" : 25 * mm, "offsetDistance" : 25 * mm});
        }
        {
            var Q0;
            Q0=makeQuery(id+"F1.opRevolve","SWEPT_FACE",FACE,{"disambiguationData":[OSD([sQuery(id+"F0.wireOp",EDGE,"E0.top")])]});
            var sketch = newSketch(context, id + "F4", { "sketchPlane" : qUnion([Q0])});
            skCircle(sketch, "E30", {"center": v(0, 0) * mm, "radius": 1.13 * mm});
            skCircle(sketch, "E31", {"center": v(0, 0) * mm, "radius": 1.38 * mm});
            skSolve(sketch);
        }
        {
            var Q0;
            Q0=makeQuery(id+"F1.opRevolve","SWEPT_FACE",FACE,{"disambiguationData":[OSD([sQuery(id+"F0.wireOp",EDGE,"E0.bottom")])]});
            var sketch = newSketch(context, id + "F5", { "sketchPlane" : qUnion([Q0])});
            skCircle(sketch, "E32.0", {"center": v(0, 0) * mm, "radius": 1.38 * mm});
            skCircle(sketch, "E33.0", {"center": v(0, 0) * mm, "radius": 1.13 * mm});
            skSolve(sketch);
        }
        {
            var Q0;
            Q0=makeQuery(id+"F5.imprint","IMPRINT",FACE,{"disambiguationData":[TD([[makeQuery(id+"F5.imprint","IMPRINT",EDGE,{"derivedFrom":sQuery(id+"F5.wireOp",EDGE,"E32.0")}),-1.0]])]});
            extrude(context, id + "F6", {"entities" : qUnion([Q0]), "operationType" : NewBodyOperationType.REMOVE, "oppositeDirection" : true, "depth" : 0.5 * mm, "offsetDistance" : 25 * mm});
        }
        {
            var Q0;
            Q0=makeQuery(id+"F4.imprint","IMPRINT",FACE,{"disambiguationData":[TD([[makeQuery(id+"F4.imprint","IMPRINT",EDGE,{"derivedFrom":sQuery(id+"F4.wireOp",EDGE,"E30")}),-1.0]])]});
            extrude(context, id + "F7", {"entities" : qUnion([Q0]), "operationType" : NewBodyOperationType.REMOVE, "oppositeDirection" : true, "depth" : 0.5 * mm, "offsetDistance" : 25 * mm});
        }
    });
